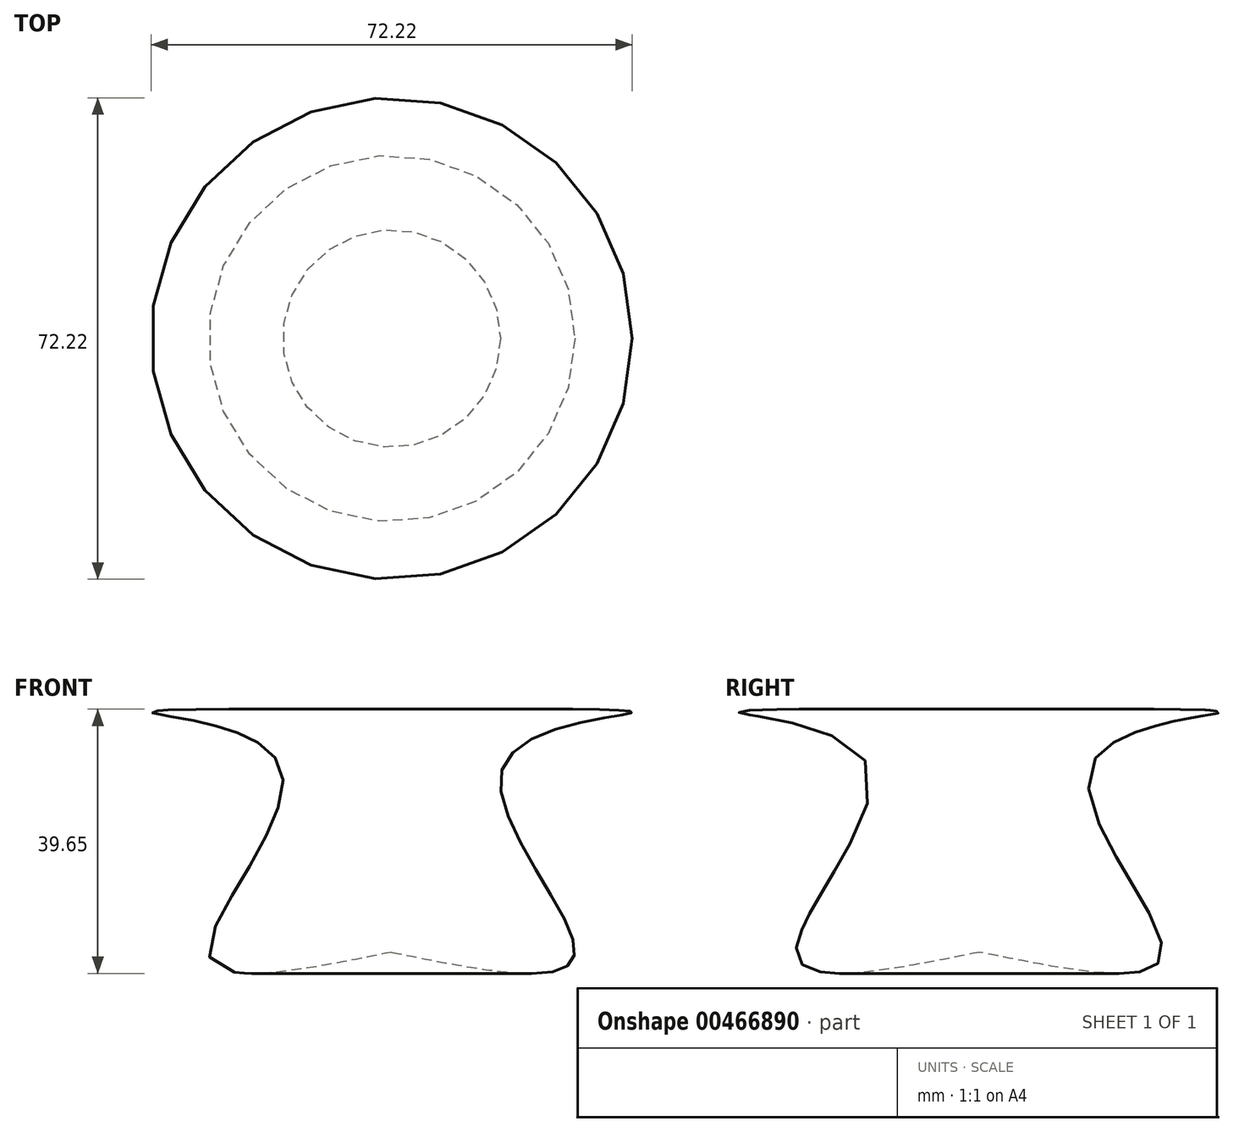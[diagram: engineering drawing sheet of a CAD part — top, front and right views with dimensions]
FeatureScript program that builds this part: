
annotation { "Feature Type Name" : "Feature", "Feature Type Description" : "" }
export const myFeature = defineFeature(function(context is Context, id is Id, definition is map)
    precondition{}
    {
        {
            var Q0;
            Q0=qCreatedBy(makeId("Front.planeOp"),FACE);
            var sketch = newSketch(context, id + "F0", { "sketchPlane" : qUnion([Q0])});
            skLineSegment(sketch, "E0", {"start": v(0, 53.12) * mm, "end": v(0, 6.52) * mm});
            skLineSegment(sketch, "E1", {"start": v(0, 6.52) * mm, "end": v(0, 0) * mm});
            skFitSpline(sketch, "E2", {"points": [v(0, 0) * mm, v(27.5, 0) * mm, v(16.77, 27.96) * mm, v(35.88, 35.88) * mm, v(0, 36.34) * mm], "startDerivative": vector(165.3, -33.51) * mm, "endDerivative": vector(-204.7, -1.69) * mm});
            skSolve(sketch);
        }
        {
            var Q0;
            {var subQ0=sQuery(id+"F0.wireOp",EDGE,"E1");Q0=makeQuery(id+"F0.imprint","IMPRINT",FACE,{"disambiguationData":[TD([[makeQuery(id+"F0.imprint","IMPRINT",EDGE,{"derivedFrom":subQ0}),1.0]])]});}
            var Q1;
            Q1=sQuery(id+"F0.wireOp",EDGE,"E0");
            revolve(context, id + "F1", {"entities" : qUnion([Q0]), "axis" : qUnion([Q1]), "revolveType" : RevolveType.FULL});
        }
    });
